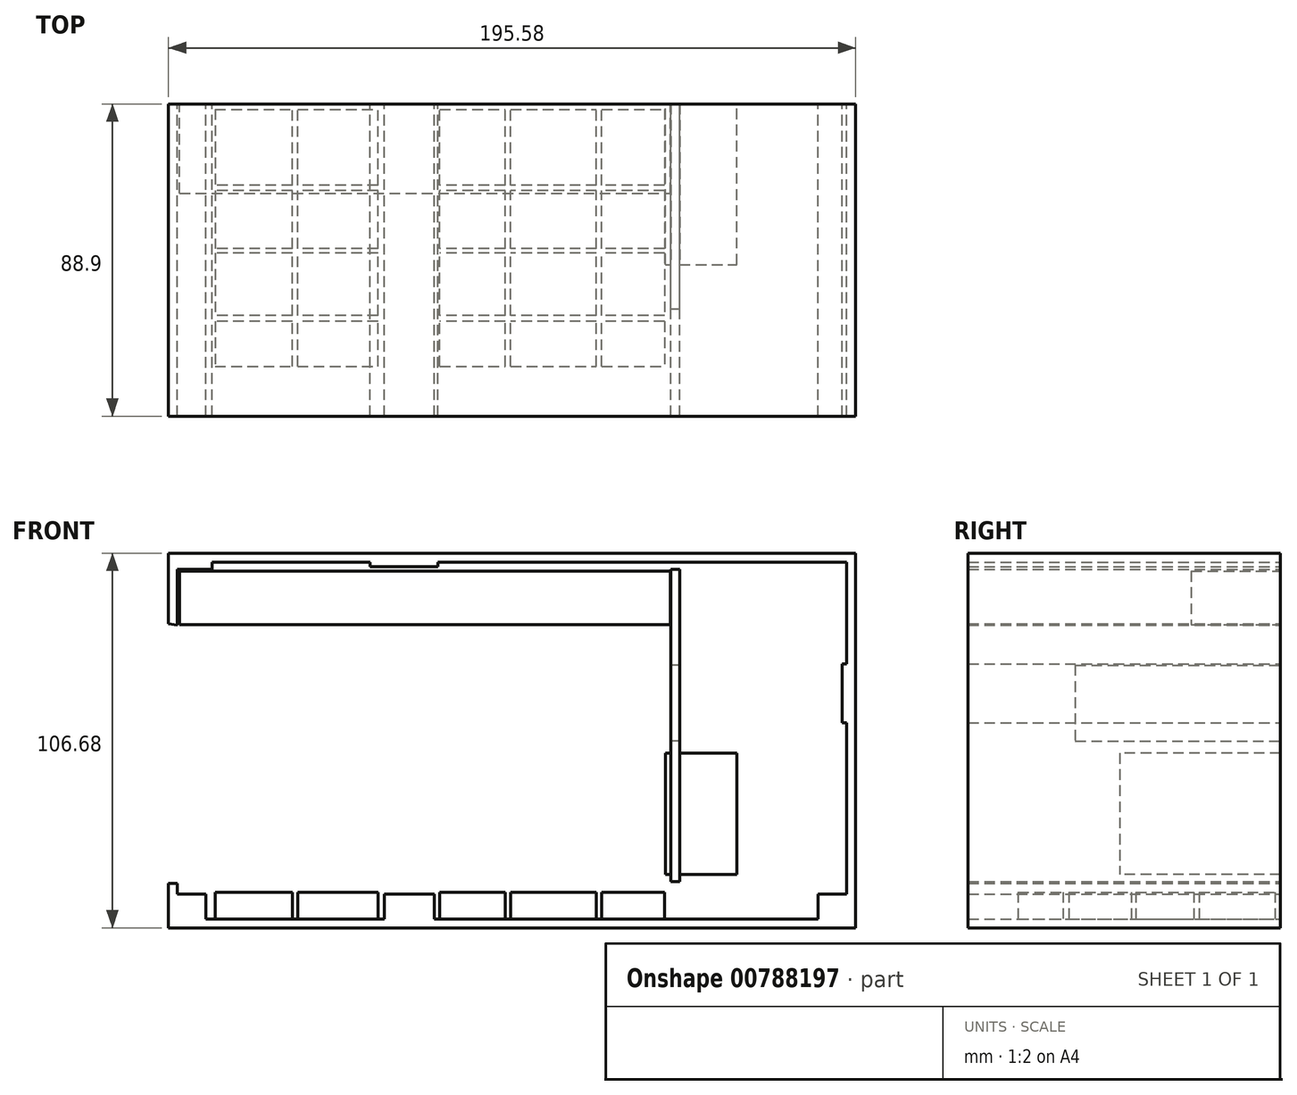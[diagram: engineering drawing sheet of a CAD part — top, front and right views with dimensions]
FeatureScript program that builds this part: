
annotation { "Feature Type Name" : "Feature", "Feature Type Description" : "" }
export const myFeature = defineFeature(function(context is Context, id is Id, definition is map)
    precondition{}
    {
        {
            var Q0;
            Q0=qCreatedBy(makeId("Front.planeOp"),FACE);
            var sketch = newSketch(context, id + "F0", { "sketchPlane" : qUnion([Q0])});
            skLineSegment(sketch, "E0.bottom", {"start": v(-54.2, 79.9) * mm, "end": v(-9.3, 79.9) * mm});
            skLineSegment(sketch, "E0.top", {"start": v(-55.99, -21.7) * mm, "end": v(-5.19, -21.7) * mm});
            skLineSegment(sketch, "E0.left", {"start": v(-64.11, 77.87) * mm, "end": v(-64.11, 61.9) * mm});
            skLineSegment(sketch, "E0.right", {"start": v(126.39, 79.9) * mm, "end": v(126.39, 50.94) * mm});
            skLineSegment(sketch, "E1.0", {"start": v(-66.65, 82.44) * mm, "end": v(128.93, 82.44) * mm});
            skLineSegment(sketch, "E1.1", {"start": v(-66.65, 82.44) * mm, "end": v(-66.65, 62.28) * mm});
            skLineSegment(sketch, "E1.2", {"start": v(-66.65, -24.24) * mm, "end": v(128.93, -24.24) * mm});
            skLineSegment(sketch, "E1.3", {"start": v(128.93, 82.44) * mm, "end": v(128.93, -24.24) * mm});
            skLineSegment(sketch, "E2.top", {"start": v(-64.11, -14.6) * mm, "end": v(-55.99, -14.6) * mm});
            skLineSegment(sketch, "E2.right", {"start": v(-55.99, -21.7) * mm, "end": v(-55.99, -14.6) * mm});
            skLineSegment(sketch, "E3.bottom", {"start": v(-5.19, -14.6) * mm, "end": v(9.04, -14.6) * mm});
            skLineSegment(sketch, "E3.left", {"start": v(-5.19, -14.6) * mm, "end": v(-5.19, -21.7) * mm});
            skLineSegment(sketch, "E3.right", {"start": v(9.04, -14.6) * mm, "end": v(9.04, -21.7) * mm});
            skLineSegment(sketch, "E4.bottom", {"start": v(134.23, -21.7) * mm, "end": v(128.93, -21.7) * mm});
            skPoint(sketch, "E4.top.end.orphan", {"position": v(118.26, -14.6) * mm});
            skLineSegment(sketch, "E5", {"start": v(-64.11, -14.6) * mm, "end": v(-64.11, -11.03) * mm, "construction": true});
            skLineSegment(sketch, "E6.top", {"start": v(-64.11, -11.54) * mm, "end": v(-66.65, -11.54) * mm});
            skLineSegment(sketch, "E7.trimOffspring", {"start": v(-64.11, -11.54) * mm, "end": v(-64.11, -14.6) * mm});
            skLineSegment(sketch, "E8.trimOffspring", {"start": v(-66.65, -11.54) * mm, "end": v(-66.65, -24.24) * mm});
            skLineSegment(sketch, "E9.top", {"start": v(-64.11, 77.87) * mm, "end": v(-54.2, 77.87) * mm});
            skLineSegment(sketch, "E9.right", {"start": v(-54.2, 79.9) * mm, "end": v(-54.2, 77.87) * mm});
            skLineSegment(sketch, "E10.top", {"start": v(-9.3, 78.63) * mm, "end": v(10, 78.63) * mm});
            skLineSegment(sketch, "E10.left", {"start": v(-9.3, 79.9) * mm, "end": v(-9.3, 78.63) * mm});
            skLineSegment(sketch, "E10.right", {"start": v(10, 79.9) * mm, "end": v(10, 78.63) * mm});
            skLineSegment(sketch, "E11.bottom", {"start": v(126.39, 34.18) * mm, "end": v(125.12, 34.18) * mm});
            skLineSegment(sketch, "E11.top", {"start": v(126.39, 50.94) * mm, "end": v(125.12, 50.94) * mm});
            skLineSegment(sketch, "E11.right", {"start": v(125.12, 34.18) * mm, "end": v(125.12, 50.94) * mm});
            skLineSegment(sketch, "E12.top", {"start": v(126.39, -14.6) * mm, "end": v(118.26, -14.6) * mm});
            skLineSegment(sketch, "E12.right", {"start": v(118.26, -21.7) * mm, "end": v(118.26, -14.6) * mm});
            skLineSegment(sketch, "E13", {"start": v(-66.65, 62.28) * mm, "end": v(-64.11, 61.9) * mm});
            skLineSegment(sketch, "E14", {"start": v(126.1, 79.9) * mm, "end": v(126.1, 51.1) * mm, "construction": true});
            skLineSegment(sketch, "E15.trimOffspring", {"start": v(10, 79.9) * mm, "end": v(126.39, 79.9) * mm});
            skLineSegment(sketch, "E16.trimOffspring", {"start": v(9.04, -21.7) * mm, "end": v(118.26, -21.7) * mm});
            skLineSegment(sketch, "E17.trimOffspring", {"start": v(126.39, 34.18) * mm, "end": v(126.39, -14.6) * mm});
            skLineSegment(sketch, "E18", {"start": v(140.18, -21.7) * mm, "end": v(140.18, -14.6) * mm, "construction": true});
            skLineSegment(sketch, "E19", {"start": v(126.39, 34.18) * mm, "end": v(126.39, -14.6) * mm, "construction": true});
            skLineSegment(sketch, "E20", {"start": v(-55.99, -21.7) * mm, "end": v(-5.19, -21.7) * mm, "construction": true});
            skLineSegment(sketch, "E21", {"start": v(9.04, -21.7) * mm, "end": v(118.26, -21.7) * mm, "construction": true});
            skPoint(sketch, "E22.start.orphan", {"position": v(-73.98, -11.54) * mm});
            skLineSegment(sketch, "E23", {"start": v(-64.11, 77.87) * mm, "end": v(-64.11, 61.9) * mm, "construction": true});
            skLineSegment(sketch, "E24", {"start": v(-66.65, -21.7) * mm, "end": v(-66.65, -11.54) * mm, "construction": true});
            skLineSegment(sketch, "E25", {"start": v(33.1, 79.9) * mm, "end": v(33.1, 21.96) * mm, "construction": true});
            skSolve(sketch);
        }
        {
            var Q0;
            Q0=qCreatedBy(makeId("Front.planeOp"),FACE);
            var sketch = newSketch(context, id + "F1", { "sketchPlane" : qUnion([Q0])});
            skLineSegment(sketch, "E26.bottom", {"start": v(-63.54, 77.3) * mm, "end": v(76.16, 77.3) * mm});
            skLineSegment(sketch, "E26.top", {"start": v(-63.54, 62.06) * mm, "end": v(76.16, 62.06) * mm});
            skLineSegment(sketch, "E26.left", {"start": v(-63.54, 77.3) * mm, "end": v(-63.54, 62.06) * mm});
            skLineSegment(sketch, "E26.right", {"start": v(76.16, 77.3) * mm, "end": v(76.16, 62.06) * mm});
            skSolve(sketch);
        }
        {
            var Q0;
            Q0=qCreatedBy(makeId("Front.planeOp"),FACE);
            var sketch = newSketch(context, id + "F2", { "sketchPlane" : qUnion([Q0])});
            skLineSegment(sketch, "E27.bottom", {"start": v(74.73, 25.5) * mm, "end": v(95.05, 25.5) * mm});
            skLineSegment(sketch, "E27.top", {"start": v(74.73, -9.04) * mm, "end": v(95.05, -9.04) * mm});
            skLineSegment(sketch, "E27.left", {"start": v(74.73, 25.5) * mm, "end": v(74.73, -9.04) * mm});
            skLineSegment(sketch, "E27.right", {"start": v(95.05, 25.5) * mm, "end": v(95.05, -9.04) * mm});
            skSolve(sketch);
        }
        {
            var Q0;
            Q0=qCreatedBy(makeId("Front.planeOp"),FACE);
            var sketch = newSketch(context, id + "F3", { "sketchPlane" : qUnion([Q0])});
            skLineSegment(sketch, "E28.bottom", {"start": v(76.27, 77.77) * mm, "end": v(78.8, 77.77) * mm});
            skLineSegment(sketch, "E28.top", {"start": v(76.27, -11.13) * mm, "end": v(78.8, -11.13) * mm});
            skLineSegment(sketch, "E28.left", {"start": v(76.27, 77.77) * mm, "end": v(76.27, -11.13) * mm});
            skLineSegment(sketch, "E28.right", {"start": v(78.8, 77.77) * mm, "end": v(78.8, -11.13) * mm});
            skPoint(sketch, "E29.bottom.start.orphan", {"position": v(78.8, 26.76) * mm});
            skSolve(sketch);
        }
        {
            var Q0;
            Q0=qCreatedBy(makeId("Front.planeOp"),FACE);
            var sketch = newSketch(context, id + "F4", { "sketchPlane" : qUnion([Q0])});
            skSolve(sketch);
        }
        {
            var Q0;
            Q0 = qSketchRegion(id + "F4", true);
            var Q1;
            Q1=makeQuery(id+"F0.imprint","IMPRINT",FACE,{"disambiguationData":[TD([[makeQuery(id+"F0.imprint","IMPRINT",EDGE,{"derivedFrom":sQuery(id+"F0.wireOp",EDGE,"E0.bottom")}),1.0]])]});
            var Q2;
            Q2=makeQuery(id+"F3.imprint","IMPRINT",FACE,{"disambiguationData":[TD([[makeQuery(id+"F3.imprint","IMPRINT",EDGE,{"derivedFrom":sQuery(id+"F3.wireOp",EDGE,"E28.bottom")}),-1.0]])]});
            var Q3;
            Q3=makeQuery(id+"F3.imprint","IMPRINT",FACE,{"disambiguationData":[TD([[makeQuery(id+"F3.imprint","IMPRINT",EDGE,{"derivedFrom":sQuery(id+"F3.wireOp",EDGE,"E29.bottom")}),1.0]])]});
            extrude(context, id + "F5", {"entities" : qUnion([Q0, Q1, Q2, Q3]), "depth" : 88.9 * mm, "offsetDistance" : 25.4 * mm});
        }
        {
            var Q0;
            Q0 = qSketchRegion(id + "F2", true);
            extrude(context, id + "F6", {"entities" : qUnion([Q0]), "operationType" : NewBodyOperationType.ADD, "depth" : 45.72 * mm, "offsetDistance" : 25.4 * mm});
        }
        {
            var Q0;
            Q0=qCreatedBy(makeId("Front.planeOp"),FACE);
            var sketch = newSketch(context, id + "F7", { "sketchPlane" : qUnion([Q0])});
            skLineSegment(sketch, "E30.bottom", {"start": v(80.06, 28.95) * mm, "end": v(74.98, 28.95) * mm});
            skLineSegment(sketch, "E30.top", {"start": v(80.06, 50.54) * mm, "end": v(74.98, 50.54) * mm});
            skLineSegment(sketch, "E30.left", {"start": v(80.06, 28.95) * mm, "end": v(80.06, 50.54) * mm});
            skLineSegment(sketch, "E30.right", {"start": v(74.98, 28.95) * mm, "end": v(74.98, 50.54) * mm});
            skSolve(sketch);
        }
        {
            var Q0;
            Q0 = qSketchRegion(id + "F1", true);
            extrude(context, id + "F8", {"entities" : qUnion([Q0]), "depth" : 25.4 * mm, "offsetDistance" : 25.4 * mm});
        }
        {
            var Q0;
            Q0 = qSketchRegion(id + "F7", true);
            extrude(context, id + "F9", {"entities" : qUnion([Q0]), "operationType" : NewBodyOperationType.REMOVE, "depth" : 58.42 * mm, "offsetDistance" : 25.4 * mm});
        }
        {
            var Q0;
            Q0 = qSketchRegion(id + "F2", true);
            extrude(context, id + "F10", {"entities" : qUnion([Q0]), "operationType" : NewBodyOperationType.ADD, "depth" : 43.18 * mm, "offsetDistance" : 25.4 * mm});
        }
        {
            var Q0;
            Q0=makeQuery(id+"F5.opExtrude","SWEPT_FACE",FACE,{"disambiguationData":[OSD([sQuery(id+"F0.wireOp",EDGE,"E16.trimOffspring")])]});
            var sketch = newSketch(context, id + "F11", { "sketchPlane" : qUnion([Q0])});
            skLineSegment(sketch, "E31.bottom", {"start": v(-54.92, 0) * mm, "end": v(76.04, 0) * mm});
            skLineSegment(sketch, "E31.top", {"start": v(-54.92, -76.2) * mm, "end": v(76.04, -76.2) * mm});
            skLineSegment(sketch, "E31.left", {"start": v(-54.92, 0) * mm, "end": v(-54.92, -76.2) * mm});
            skLineSegment(sketch, "E31.right", {"start": v(76.04, 0) * mm, "end": v(76.04, -76.2) * mm});
            skLineSegment(sketch, "E32.MirrorCS", {"start": v(76.04, -152.4) * mm, "end": v(76.04, -76.2) * mm});
            skLineSegment(sketch, "E33.MirrorCS", {"start": v(-54.92, -152.4) * mm, "end": v(76.04, -152.4) * mm});
            skLineSegment(sketch, "E34.MirrorCS", {"start": v(-54.92, -152.4) * mm, "end": v(-54.92, -76.2) * mm});
            skLineSegment(sketch, "E35.0", {"start": v(-53.4, -74.68) * mm, "end": v(74.52, -74.68) * mm});
            skLineSegment(sketch, "E35.1", {"start": v(-53.4, -1.52) * mm, "end": v(-53.4, -74.68) * mm});
            skLineSegment(sketch, "E35.2", {"start": v(-53.4, -1.52) * mm, "end": v(74.52, -1.52) * mm});
            skLineSegment(sketch, "E35.3", {"start": v(74.52, -1.52) * mm, "end": v(74.52, -74.68) * mm});
            skLineSegment(sketch, "E36.bottom", {"start": v(-5.5, -76.2) * mm, "end": v(-7.02, -76.2) * mm});
            skLineSegment(sketch, "E36.top", {"start": v(-5.5, 0) * mm, "end": v(-7.02, 0) * mm});
            skLineSegment(sketch, "E36.left", {"start": v(-5.5, -76.2) * mm, "end": v(-5.5, 0) * mm});
            skLineSegment(sketch, "E36.right", {"start": v(-7.02, -76.2) * mm, "end": v(-7.02, 0) * mm});
            skLineSegment(sketch, "E37.bottom", {"start": v(9.04, -76.2) * mm, "end": v(10.56, -76.2) * mm});
            skLineSegment(sketch, "E37.top", {"start": v(9.04, 0) * mm, "end": v(10.56, 0) * mm});
            skLineSegment(sketch, "E37.left", {"start": v(9.04, -76.2) * mm, "end": v(9.04, 0) * mm});
            skLineSegment(sketch, "E37.right", {"start": v(10.56, -76.2) * mm, "end": v(10.56, 0) * mm});
            skLineSegment(sketch, "E38.bottom", {"start": v(-29.93, -76.2) * mm, "end": v(-31.46, -76.2) * mm});
            skLineSegment(sketch, "E38.top", {"start": v(-29.93, 0) * mm, "end": v(-31.46, 0) * mm});
            skLineSegment(sketch, "E38.left", {"start": v(-29.93, -76.2) * mm, "end": v(-29.93, 0) * mm});
            skLineSegment(sketch, "E38.right", {"start": v(-31.46, -76.2) * mm, "end": v(-31.46, 0) * mm});
            skLineSegment(sketch, "E39.bottom", {"start": v(30.7, -76.2) * mm, "end": v(29.18, -76.2) * mm});
            skLineSegment(sketch, "E39.top", {"start": v(30.7, 0) * mm, "end": v(29.18, 0) * mm});
            skLineSegment(sketch, "E39.left", {"start": v(30.7, -76.2) * mm, "end": v(30.7, 0) * mm});
            skLineSegment(sketch, "E39.right", {"start": v(29.18, -76.2) * mm, "end": v(29.18, 0) * mm});
            skLineSegment(sketch, "E40.bottom", {"start": v(56.66, -76.2) * mm, "end": v(55.13, -76.2) * mm});
            skLineSegment(sketch, "E40.top", {"start": v(56.66, 0) * mm, "end": v(55.13, 0) * mm});
            skLineSegment(sketch, "E40.left", {"start": v(56.66, -76.2) * mm, "end": v(56.66, 0) * mm});
            skLineSegment(sketch, "E40.right", {"start": v(55.13, -76.2) * mm, "end": v(55.13, 0) * mm});
            skLineSegment(sketch, "E41.bottom", {"start": v(74.52, -61.93) * mm, "end": v(-53.4, -61.93) * mm});
            skLineSegment(sketch, "E41.top", {"start": v(74.52, -60.26) * mm, "end": v(-53.4, -60.26) * mm});
            skLineSegment(sketch, "E41.left", {"start": v(74.52, -61.93) * mm, "end": v(74.52, -60.26) * mm});
            skLineSegment(sketch, "E41.right", {"start": v(-53.4, -61.93) * mm, "end": v(-53.4, -60.26) * mm});
            skLineSegment(sketch, "E42.bottom", {"start": v(74.52, -42.46) * mm, "end": v(-53.4, -42.46) * mm});
            skLineSegment(sketch, "E42.top", {"start": v(74.52, -41.17) * mm, "end": v(-53.4, -41.17) * mm});
            skLineSegment(sketch, "E42.left", {"start": v(74.52, -42.46) * mm, "end": v(74.52, -41.17) * mm});
            skLineSegment(sketch, "E42.right", {"start": v(-53.4, -42.46) * mm, "end": v(-53.4, -41.17) * mm});
            skLineSegment(sketch, "E43.bottom", {"start": v(74.52, -24.66) * mm, "end": v(-53.4, -24.66) * mm});
            skLineSegment(sketch, "E43.top", {"start": v(74.52, -23.18) * mm, "end": v(-53.4, -23.18) * mm});
            skLineSegment(sketch, "E43.left", {"start": v(74.52, -24.66) * mm, "end": v(74.52, -23.18) * mm});
            skLineSegment(sketch, "E43.right", {"start": v(-53.4, -24.66) * mm, "end": v(-53.4, -23.18) * mm});
            skSolve(sketch);
        }
        {
            var Q0;
            {var subQ0=sQuery(id+"F11.wireOp",EDGE,"E35.1");var subQ1=sQuery(id+"F11.wireOp",EDGE,"E35.0");var subQ2=makeQuery(id+"F11.imprint","INTERSECT",VERTEX,{"derivedFrom":[subQ1,subQ0]});Q0=makeQuery(id+"F11.imprint","IMPRINT",FACE,{"disambiguationData":[TD([[makeQuery(id+"F11.imprint","IMPRINT",EDGE,{"disambiguationData":[TD([[subQ2,-1.0]])],"derivedFrom":subQ1}),1.0]])]});}
            var Q1;
            {var subQ0=sQuery(id+"F11.wireOp",EDGE,"E41.top");var subQ5=sQuery(id+"F11.wireOp",EDGE,"E38.right");var subQ6=makeQuery(id+"F11.imprint","INTERSECT",VERTEX,{"derivedFrom":[subQ5,subQ0]});Q1=makeQuery(id+"F11.imprint","IMPRINT",FACE,{"disambiguationData":[TD([[makeQuery(id+"F11.imprint","IMPRINT",EDGE,{"disambiguationData":[TD([[subQ6,-1.0]])],"derivedFrom":subQ5}),1.0]])]});}
            var Q2;
            {var subQ0=sQuery(id+"F11.wireOp",EDGE,"E41.top");var subQ1=sQuery(id+"F11.wireOp",EDGE,"E36.right");var subQ2=makeQuery(id+"F11.imprint","INTERSECT",VERTEX,{"derivedFrom":[subQ1,subQ0]});Q2=makeQuery(id+"F11.imprint","IMPRINT",FACE,{"disambiguationData":[TD([[makeQuery(id+"F11.imprint","IMPRINT",EDGE,{"disambiguationData":[TD([[subQ2,-1.0]])],"derivedFrom":subQ1}),1.0]])]});}
            var Q3;
            {var subQ0=sQuery(id+"F11.wireOp",EDGE,"E38.left");var subQ1=sQuery(id+"F11.wireOp",EDGE,"E35.0");var subQ2=makeQuery(id+"F11.imprint","INTERSECT",VERTEX,{"derivedFrom":[subQ1,subQ0]});Q3=makeQuery(id+"F11.imprint","IMPRINT",FACE,{"disambiguationData":[TD([[makeQuery(id+"F11.imprint","IMPRINT",EDGE,{"disambiguationData":[TD([[subQ2,-1.0]])],"derivedFrom":subQ1}),1.0]])]});}
            var Q4;
            {var subQ0=sQuery(id+"F11.wireOp",EDGE,"E42.top");var subQ5=sQuery(id+"F11.wireOp",EDGE,"E38.right");var subQ6=makeQuery(id+"F11.imprint","INTERSECT",VERTEX,{"derivedFrom":[subQ5,subQ0]});Q4=makeQuery(id+"F11.imprint","IMPRINT",FACE,{"disambiguationData":[TD([[makeQuery(id+"F11.imprint","IMPRINT",EDGE,{"disambiguationData":[TD([[subQ6,-1.0]])],"derivedFrom":subQ5}),1.0]])]});}
            var Q5;
            {var subQ0=sQuery(id+"F11.wireOp",EDGE,"E42.top");var subQ1=sQuery(id+"F11.wireOp",EDGE,"E36.right");var subQ2=makeQuery(id+"F11.imprint","INTERSECT",VERTEX,{"derivedFrom":[subQ1,subQ0]});Q5=makeQuery(id+"F11.imprint","IMPRINT",FACE,{"disambiguationData":[TD([[makeQuery(id+"F11.imprint","IMPRINT",EDGE,{"disambiguationData":[TD([[subQ2,-1.0]])],"derivedFrom":subQ1}),1.0]])]});}
            var Q6;
            {var subQ0=sQuery(id+"F11.wireOp",EDGE,"E38.left");var subQ1=sQuery(id+"F11.wireOp",EDGE,"E35.2");var subQ2=makeQuery(id+"F11.imprint","INTERSECT",VERTEX,{"derivedFrom":[subQ1,subQ0]});Q6=makeQuery(id+"F11.imprint","IMPRINT",FACE,{"disambiguationData":[TD([[makeQuery(id+"F11.imprint","IMPRINT",EDGE,{"disambiguationData":[TD([[subQ2,-1.0]])],"derivedFrom":subQ1}),-1.0]])]});}
            var Q7;
            {var subQ0=sQuery(id+"F11.wireOp",EDGE,"E35.2");var subQ1=sQuery(id+"F11.wireOp",EDGE,"E35.1");var subQ2=makeQuery(id+"F11.imprint","INTERSECT",VERTEX,{"derivedFrom":[subQ1,subQ0]});Q7=makeQuery(id+"F11.imprint","IMPRINT",FACE,{"disambiguationData":[TD([[makeQuery(id+"F11.imprint","IMPRINT",EDGE,{"disambiguationData":[TD([[subQ2,-1.0]])],"derivedFrom":subQ0}),-1.0]])]});}
            var Q8;
            {var subQ0=sQuery(id+"F11.wireOp",EDGE,"E42.top");var subQ1=sQuery(id+"F11.wireOp",EDGE,"E37.right");var subQ2=makeQuery(id+"F11.imprint","INTERSECT",VERTEX,{"derivedFrom":[subQ1,subQ0]});Q8=makeQuery(id+"F11.imprint","IMPRINT",FACE,{"disambiguationData":[TD([[makeQuery(id+"F11.imprint","IMPRINT",EDGE,{"disambiguationData":[TD([[subQ2,-1.0]])],"derivedFrom":subQ1}),-1.0]])]});}
            var Q9;
            {var subQ0=sQuery(id+"F11.wireOp",EDGE,"E41.top");var subQ1=sQuery(id+"F11.wireOp",EDGE,"E37.right");var subQ2=makeQuery(id+"F11.imprint","INTERSECT",VERTEX,{"derivedFrom":[subQ1,subQ0]});Q9=makeQuery(id+"F11.imprint","IMPRINT",FACE,{"disambiguationData":[TD([[makeQuery(id+"F11.imprint","IMPRINT",EDGE,{"disambiguationData":[TD([[subQ2,-1.0]])],"derivedFrom":subQ1}),-1.0]])]});}
            var Q10;
            {var subQ0=sQuery(id+"F11.wireOp",EDGE,"E37.right");var subQ1=sQuery(id+"F11.wireOp",EDGE,"E35.0");var subQ2=makeQuery(id+"F11.imprint","INTERSECT",VERTEX,{"derivedFrom":[subQ1,subQ0]});Q10=makeQuery(id+"F11.imprint","IMPRINT",FACE,{"disambiguationData":[TD([[makeQuery(id+"F11.imprint","IMPRINT",EDGE,{"disambiguationData":[TD([[subQ2,-1.0]])],"derivedFrom":subQ1}),1.0]])]});}
            var Q11;
            {var subQ0=sQuery(id+"F11.wireOp",EDGE,"E39.left");var subQ1=sQuery(id+"F11.wireOp",EDGE,"E35.0");var subQ2=makeQuery(id+"F11.imprint","INTERSECT",VERTEX,{"derivedFrom":[subQ1,subQ0]});Q11=makeQuery(id+"F11.imprint","IMPRINT",FACE,{"disambiguationData":[TD([[makeQuery(id+"F11.imprint","IMPRINT",EDGE,{"disambiguationData":[TD([[subQ2,-1.0]])],"derivedFrom":subQ1}),1.0]])]});}
            var Q12;
            {var subQ0=sQuery(id+"F11.wireOp",EDGE,"E35.3");var subQ1=sQuery(id+"F11.wireOp",EDGE,"E35.0");var subQ2=makeQuery(id+"F11.imprint","INTERSECT",VERTEX,{"derivedFrom":[subQ1,subQ0]});Q12=makeQuery(id+"F11.imprint","IMPRINT",FACE,{"disambiguationData":[TD([[makeQuery(id+"F11.imprint","IMPRINT",EDGE,{"disambiguationData":[TD([[subQ2,1.0]])],"derivedFrom":subQ1}),1.0]])]});}
            var Q13;
            {var subQ0=sQuery(id+"F11.wireOp",EDGE,"E41.top");var subQ5=sQuery(id+"F11.wireOp",EDGE,"E40.left");var subQ6=makeQuery(id+"F11.imprint","INTERSECT",VERTEX,{"derivedFrom":[subQ5,subQ0]});Q13=makeQuery(id+"F11.imprint","IMPRINT",FACE,{"disambiguationData":[TD([[makeQuery(id+"F11.imprint","IMPRINT",EDGE,{"disambiguationData":[TD([[subQ6,-1.0]])],"derivedFrom":subQ5}),-1.0]])]});}
            var Q14;
            {var subQ0=sQuery(id+"F11.wireOp",EDGE,"E41.top");var subQ1=sQuery(id+"F11.wireOp",EDGE,"E39.left");var subQ2=makeQuery(id+"F11.imprint","INTERSECT",VERTEX,{"derivedFrom":[subQ1,subQ0]});Q14=makeQuery(id+"F11.imprint","IMPRINT",FACE,{"disambiguationData":[TD([[makeQuery(id+"F11.imprint","IMPRINT",EDGE,{"disambiguationData":[TD([[subQ2,-1.0]])],"derivedFrom":subQ1}),-1.0]])]});}
            var Q15;
            {var subQ0=sQuery(id+"F11.wireOp",EDGE,"E42.top");var subQ1=sQuery(id+"F11.wireOp",EDGE,"E39.left");var subQ2=makeQuery(id+"F11.imprint","INTERSECT",VERTEX,{"derivedFrom":[subQ1,subQ0]});Q15=makeQuery(id+"F11.imprint","IMPRINT",FACE,{"disambiguationData":[TD([[makeQuery(id+"F11.imprint","IMPRINT",EDGE,{"disambiguationData":[TD([[subQ2,-1.0]])],"derivedFrom":subQ1}),-1.0]])]});}
            var Q16;
            {var subQ0=sQuery(id+"F11.wireOp",EDGE,"E42.top");var subQ5=sQuery(id+"F11.wireOp",EDGE,"E40.left");var subQ6=makeQuery(id+"F11.imprint","INTERSECT",VERTEX,{"derivedFrom":[subQ5,subQ0]});Q16=makeQuery(id+"F11.imprint","IMPRINT",FACE,{"disambiguationData":[TD([[makeQuery(id+"F11.imprint","IMPRINT",EDGE,{"disambiguationData":[TD([[subQ6,-1.0]])],"derivedFrom":subQ5}),-1.0]])]});}
            var Q17;
            {var subQ0=sQuery(id+"F11.wireOp",EDGE,"E35.3");var subQ1=sQuery(id+"F11.wireOp",EDGE,"E35.2");var subQ2=makeQuery(id+"F11.imprint","INTERSECT",VERTEX,{"derivedFrom":[subQ1,subQ0]});Q17=makeQuery(id+"F11.imprint","IMPRINT",FACE,{"disambiguationData":[TD([[makeQuery(id+"F11.imprint","IMPRINT",EDGE,{"disambiguationData":[TD([[subQ2,1.0]])],"derivedFrom":subQ1}),-1.0]])]});}
            var Q18;
            {var subQ0=sQuery(id+"F11.wireOp",EDGE,"E39.left");var subQ1=sQuery(id+"F11.wireOp",EDGE,"E35.2");var subQ2=makeQuery(id+"F11.imprint","INTERSECT",VERTEX,{"derivedFrom":[subQ1,subQ0]});Q18=makeQuery(id+"F11.imprint","IMPRINT",FACE,{"disambiguationData":[TD([[makeQuery(id+"F11.imprint","IMPRINT",EDGE,{"disambiguationData":[TD([[subQ2,-1.0]])],"derivedFrom":subQ1}),-1.0]])]});}
            var Q19;
            {var subQ0=sQuery(id+"F11.wireOp",EDGE,"E37.right");var subQ1=sQuery(id+"F11.wireOp",EDGE,"E35.2");var subQ2=makeQuery(id+"F11.imprint","INTERSECT",VERTEX,{"derivedFrom":[subQ1,subQ0]});Q19=makeQuery(id+"F11.imprint","IMPRINT",FACE,{"disambiguationData":[TD([[makeQuery(id+"F11.imprint","IMPRINT",EDGE,{"disambiguationData":[TD([[subQ2,-1.0]])],"derivedFrom":subQ1}),-1.0]])]});}
            extrude(context, id + "F12", {"entities" : qUnion([Q0, Q1, Q2, Q3, Q4, Q5, Q6, Q7, Q8, Q9, Q10, Q11, Q12, Q13, Q14, Q15, Q16, Q17, Q18, Q19]), "operationType" : NewBodyOperationType.ADD, "depth" : 7.62 * mm, "offsetDistance" : 25.4 * mm});
        }
    });
